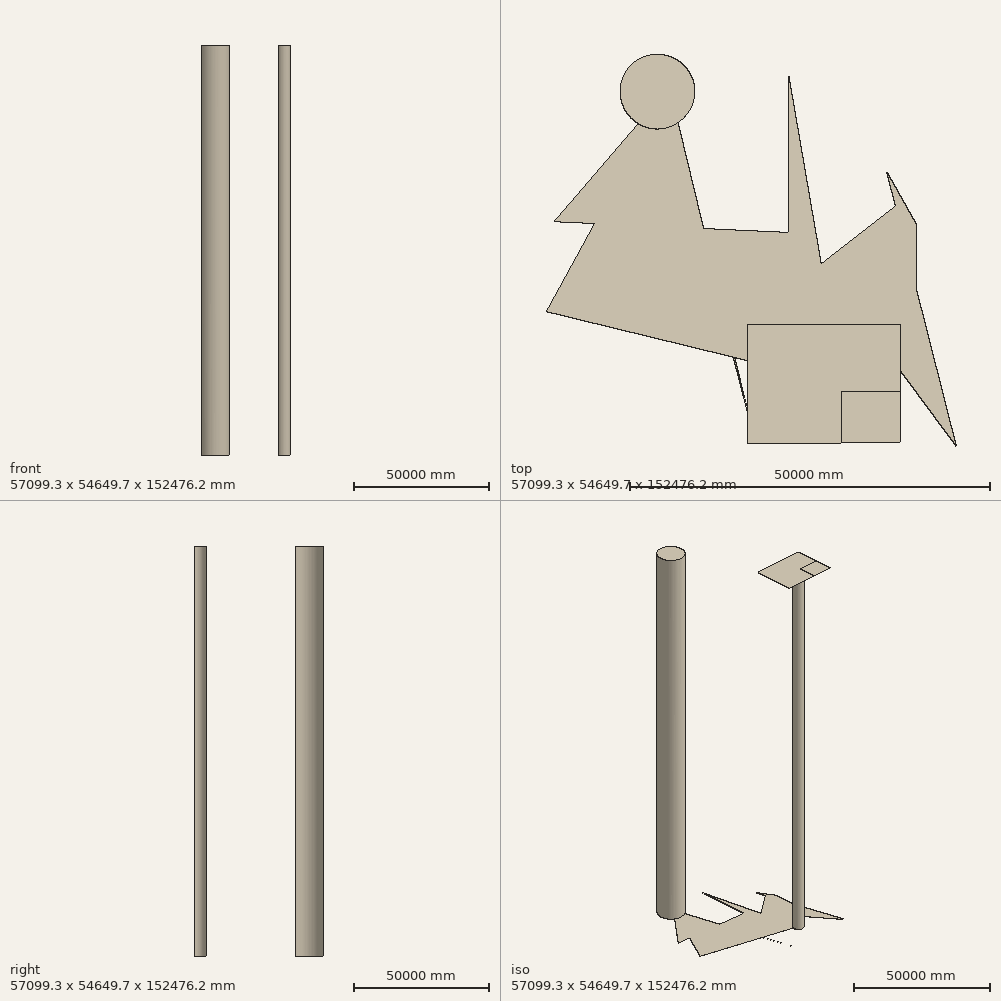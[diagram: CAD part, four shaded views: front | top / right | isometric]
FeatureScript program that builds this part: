
annotation { "Feature Type Name" : "Feature", "Feature Type Description" : "" }
export const myFeature = defineFeature(function(context is Context, id is Id, definition is map)
    precondition{}
    {
        {
            var Q0;
            Q0=qCreatedBy(makeId("Top.planeOp"),FACE);
            var sketch = newSketch(context, id + "F0", { "sketchPlane" : qUnion([Q0])});
            skCircle(sketch, "E0", {"center": v(0, 0) * mm, "radius": 2235.2 * mm});
            skSolve(sketch);
        }
        {
            var Q0;
            Q0=makeQuery(id+"F0.imprint","IMPRINT",FACE,{"disambiguationData":[TD([[makeQuery(id+"F0.imprint","IMPRINT",EDGE,{"derivedFrom":sQuery(id+"F0.wireOp",EDGE,"E0")}),1.0]])]});
            extrude(context, id + "F1", {"entities" : qUnion([Q0]), "depth" : 152400 * mm, "offsetDistance" : 25.4 * mm});
        }
        {
            var Q0;
            Q0=makeQuery(id+"F1.opExtrude","CAP_FACE",FACE,{"disambiguationData":[OSD([sQuery(id+"F0.wireOp",EDGE,"E0")])],"isStart":false});
            var sketch = newSketch(context, id + "F2", { "sketchPlane" : qUnion([Q0])});
            skLineSegment(sketch, "E1.bottom", {"start": v(-8160.04, 8175.66) * mm, "end": v(8154.04, 8175.66) * mm});
            skLineSegment(sketch, "E1.top", {"start": v(-8160.04, -8255.03) * mm, "end": v(8154.04, -8255.03) * mm});
            skLineSegment(sketch, "E1.left", {"start": v(-8160.04, 8175.66) * mm, "end": v(-8160.04, -8255.03) * mm});
            skLineSegment(sketch, "E1.right", {"start": v(8154.04, 8175.66) * mm, "end": v(8154.04, -8255.03) * mm});
            skSolve(sketch);
        }
        {
            var Q0;
            Q0 = qSketchRegion(id + "F2", true);
            extrude(context, id + "F3", {"entities" : qUnion([Q0]), "operationType" : NewBodyOperationType.ADD, "depth" : 25.4 * mm, "offsetDistance" : 25.4 * mm});
        }
        {
            var Q0;
            Q0=makeQuery(id+"F3.opExtrude","CAP_FACE",FACE,{"disambiguationData":[OSD([sQuery(id+"F2.wireOp",EDGE,"E1.bottom"),sQuery(id+"F2.wireOp",EDGE,"E1.top"),sQuery(id+"F2.wireOp",EDGE,"E1.left"),sQuery(id+"F2.wireOp",EDGE,"E1.right")])],"isStart":false});
            var sketch = newSketch(context, id + "F4", { "sketchPlane" : qUnion([Q0])});
            skLineSegment(sketch, "E2.bottom", {"start": v(0, -1081.62) * mm, "end": v(-13162.3, -1081.62) * mm});
            skLineSegment(sketch, "E2.top", {"start": v(0, -8278.2) * mm, "end": v(-13162.3, -8278.2) * mm});
            skLineSegment(sketch, "E2.left", {"start": v(0, -1081.62) * mm, "end": v(0, -8278.2) * mm});
            skLineSegment(sketch, "E2.right", {"start": v(-13162.3, -1081.62) * mm, "end": v(-13162.3, -8278.2) * mm});
            skLineSegment(sketch, "E3.bottom", {"start": v(-13162.3, -1081.62) * mm, "end": v(8154.04, -1081.62) * mm});
            skLineSegment(sketch, "E3.top", {"start": v(-13162.3, 8175.66) * mm, "end": v(8154.04, 8175.66) * mm});
            skLineSegment(sketch, "E3.left", {"start": v(-13162.3, -1081.62) * mm, "end": v(-13162.3, 8175.66) * mm});
            skLineSegment(sketch, "E3.right", {"start": v(8154.04, -1081.62) * mm, "end": v(8154.04, 8175.66) * mm});
            skSolve(sketch);
        }
        {
            var Q0;
            Q0 = qSketchRegion(id + "F4", true);
            extrude(context, id + "F5", {"entities" : qUnion([Q0]), "operationType" : NewBodyOperationType.ADD, "depth" : 25.4 * mm, "offsetDistance" : 25.4 * mm});
        }
        {
            var Q0;
            Q0=makeQuery(id+"F3.opExtrude","CAP_FACE",FACE,{"disambiguationData":[OSD([sQuery(id+"F2.wireOp",EDGE,"E1.bottom"),sQuery(id+"F2.wireOp",EDGE,"E1.top"),sQuery(id+"F2.wireOp",EDGE,"E1.left"),sQuery(id+"F2.wireOp",EDGE,"E1.right")])],"isStart":true});
            var sketch = newSketch(context, id + "F6", { "sketchPlane" : qUnion([Q0])});
            skCircle(sketch, "E4", {"center": v(-25685.07, -40658.64) * mm, "radius": 5206.75 * mm});
            skSolve(sketch);
        }
        {
            var Q0;
            Q0 = qSketchRegion(id + "F6", true);
            var Q1;
            Q1=makeQuery(id+"F1.opExtrude","CAP_FACE",FACE,{"disambiguationData":[OSD([sQuery(id+"F0.wireOp",EDGE,"E0")])],"isStart":true});
            extrude(context, id + "F7", {"entities" : qUnion([Q0]), "endBound" : BoundingType.UP_TO_SURFACE, "depth" : 25.4 * mm, "endBoundEntityFace" : qUnion([Q1]), "offsetDistance" : 25.4 * mm});
        }
        {
            var Q0;
            Q0=makeQuery(id+"F7.opExtrude","CAP_FACE",FACE,{"disambiguationData":[OSD([sQuery(id+"F6.wireOp",EDGE,"E4")])],"isStart":false});
            var sketch = newSketch(context, id + "F8", { "sketchPlane" : qUnion([Q0])});
            skLineSegment(sketch, "E5.bottom", {"start": v(-24103.8, -41115.15) * mm, "end": v(-23973.38, -41115.15) * mm});
            skLineSegment(sketch, "E5.top", {"start": v(-24103.8, -37651.04) * mm, "end": v(-23973.38, -37651.04) * mm});
            skLineSegment(sketch, "E5.left", {"start": v(-24103.8, -41115.15) * mm, "end": v(-24103.8, -37651.04) * mm});
            skLineSegment(sketch, "E5.right", {"start": v(-23973.38, -41115.15) * mm, "end": v(-23973.38, -37651.04) * mm});
            skLineSegment(sketch, "E6", {"start": v(-40052.18, -22552.81) * mm, "end": v(-7381.23, -21054.95) * mm});
            skLineSegment(sketch, "E7", {"start": v(-7381.23, -21054.95) * mm, "end": v(-7381.23, -42754.92) * mm});
            skLineSegment(sketch, "E8", {"start": v(-7381.23, -42754.92) * mm, "end": v(0, 0) * mm});
            skLineSegment(sketch, "E9", {"start": v(0, 0) * mm, "end": v(-7381.23, -21054.95) * mm});
            skLineSegment(sketch, "E10", {"start": v(-40052.18, -22552.81) * mm, "end": v(-24103.8, -41115.15) * mm});
            skLineSegment(sketch, "E11", {"start": v(-23973.38, -37651.04) * mm, "end": v(-12005.97, 8436.8) * mm});
            skLineSegment(sketch, "E12", {"start": v(-12005.97, 8436.8) * mm, "end": v(-23973.38, -41115.15) * mm});
            skLineSegment(sketch, "E13", {"start": v(10348.13, -14536.7) * mm, "end": v(10348.13, -12262.65) * mm});
            skLineSegment(sketch, "E14", {"start": v(10348.13, -12262.65) * mm, "end": v(-2874.08, -16647.76) * mm});
            skLineSegment(sketch, "E15", {"start": v(-2874.08, -16647.76) * mm, "end": v(15950.07, 8784.29) * mm});
            skLineSegment(sketch, "E16", {"start": v(15950.07, 8784.29) * mm, "end": v(6189.89, -29607.7) * mm});
            skLineSegment(sketch, "E17", {"start": v(6189.89, -29607.7) * mm, "end": v(10348.13, -22246) * mm});
            skLineSegment(sketch, "E18", {"start": v(10348.13, -22246) * mm, "end": v(10348.13, -14536.7) * mm});
            skLineSegment(sketch, "E19", {"start": v(7441.09, -24686.06) * mm, "end": v(-2874.08, -16647.76) * mm});
            skLineSegment(sketch, "E20", {"start": v(-41149.23, -10022.57) * mm, "end": v(0, 0) * mm});
            skLineSegment(sketch, "E21", {"start": v(0, 0) * mm, "end": v(5075.74, -5907.29) * mm});
            skLineSegment(sketch, "E22", {"start": v(5075.74, -5907.29) * mm, "end": v(-41149.23, -10022.57) * mm});
            skLineSegment(sketch, "E23", {"start": v(-41149.23, -10022.57) * mm, "end": v(-24103.8, -41115.15) * mm});
            skSolve(sketch);
        }
        {
            var Q0;
            Q0 = qSketchRegion(id + "F8", true);
            extrude(context, id + "F9", {"entities" : qUnion([Q0]), "depth" : 25.4 * mm, "offsetDistance" : 25.4 * mm});
        }
        {
            var Q0;
            Q0 = qSketchRegion(id + "F0", true);
            extrude(context, id + "F10", {"entities" : qUnion([Q0]), "depth" : 25.4 * mm, "offsetDistance" : 25.4 * mm});
        }
    });
